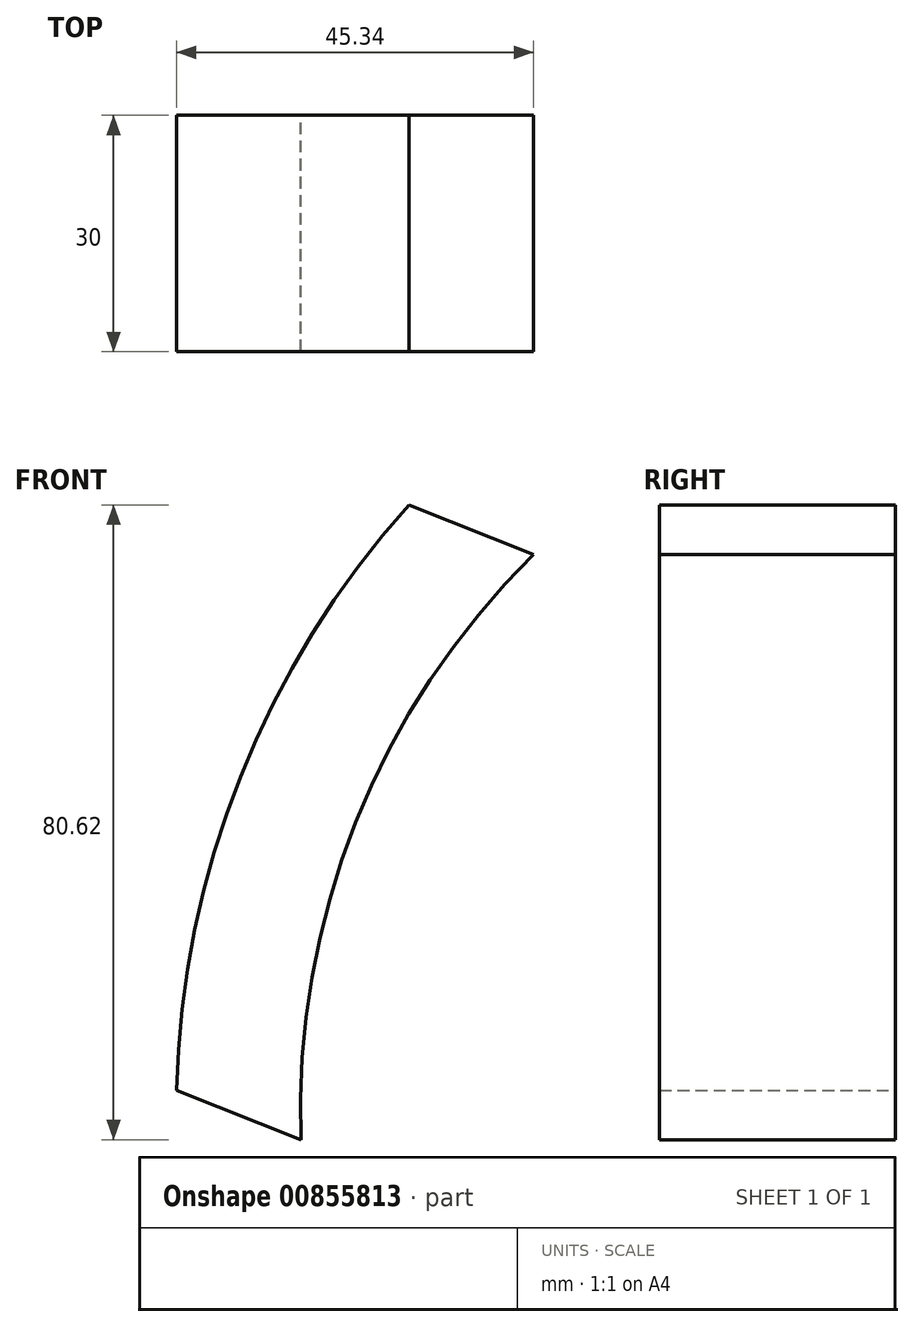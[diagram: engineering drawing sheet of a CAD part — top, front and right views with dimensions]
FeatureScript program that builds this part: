
annotation { "Feature Type Name" : "Feature", "Feature Type Description" : "" }
export const myFeature = defineFeature(function(context is Context, id is Id, definition is map)
    precondition{}
    {
        {
            var Q0;
            Q0=qCreatedBy(makeId("Front.planeOp"),FACE);
            var sketch = newSketch(context, id + "F0", { "sketchPlane" : qUnion([Q0])});
            skLineSegment(sketch, "E0", {"start": v(-20.28, 52.03) * mm, "end": v(-49.82, -22.32) * mm});
            skArc(sketch, "E1", {"start": v(-20.28, 52.03) * mm, "mid": v(-41.72, 17.5) * mm, "end": v(-49.82, -22.32) * mm});
            skLineSegment(sketch, "E2", {"start": v(-20.28, 52.03) * mm, "end": v(-4.48, 45.75) * mm});
            skLineSegment(sketch, "E3", {"start": v(-49.82, -22.32) * mm, "end": v(-34.02, -28.6) * mm});
            skArc(sketch, "E4", {"start": v(-4.48, 45.75) * mm, "mid": v(-27.08, 11.69) * mm, "end": v(-34.02, -28.6) * mm});
            skSolve(sketch);
        }
        {
            var Q0;
            Q0=makeQuery(id+"F0.imprint","IMPRINT",FACE,{"disambiguationData":[TD([[makeQuery(id+"F0.imprint","IMPRINT",EDGE,{"derivedFrom":sQuery(id+"F0.wireOp",EDGE,"E0")}),-1.0]])]});
            var Q1;
            Q1=makeQuery(id+"F0.imprint","IMPRINT",FACE,{"disambiguationData":[TD([[makeQuery(id+"F0.imprint","IMPRINT",EDGE,{"derivedFrom":sQuery(id+"F0.wireOp",EDGE,"E0")}),1.0]])]});
            extrude(context, id + "F1", {"entities" : qUnion([Q0, Q1]), "endBound" : BoundingType.SYMMETRIC, "depth" : 30 * mm, "offsetDistance" : 25 * mm});
        }
    });
